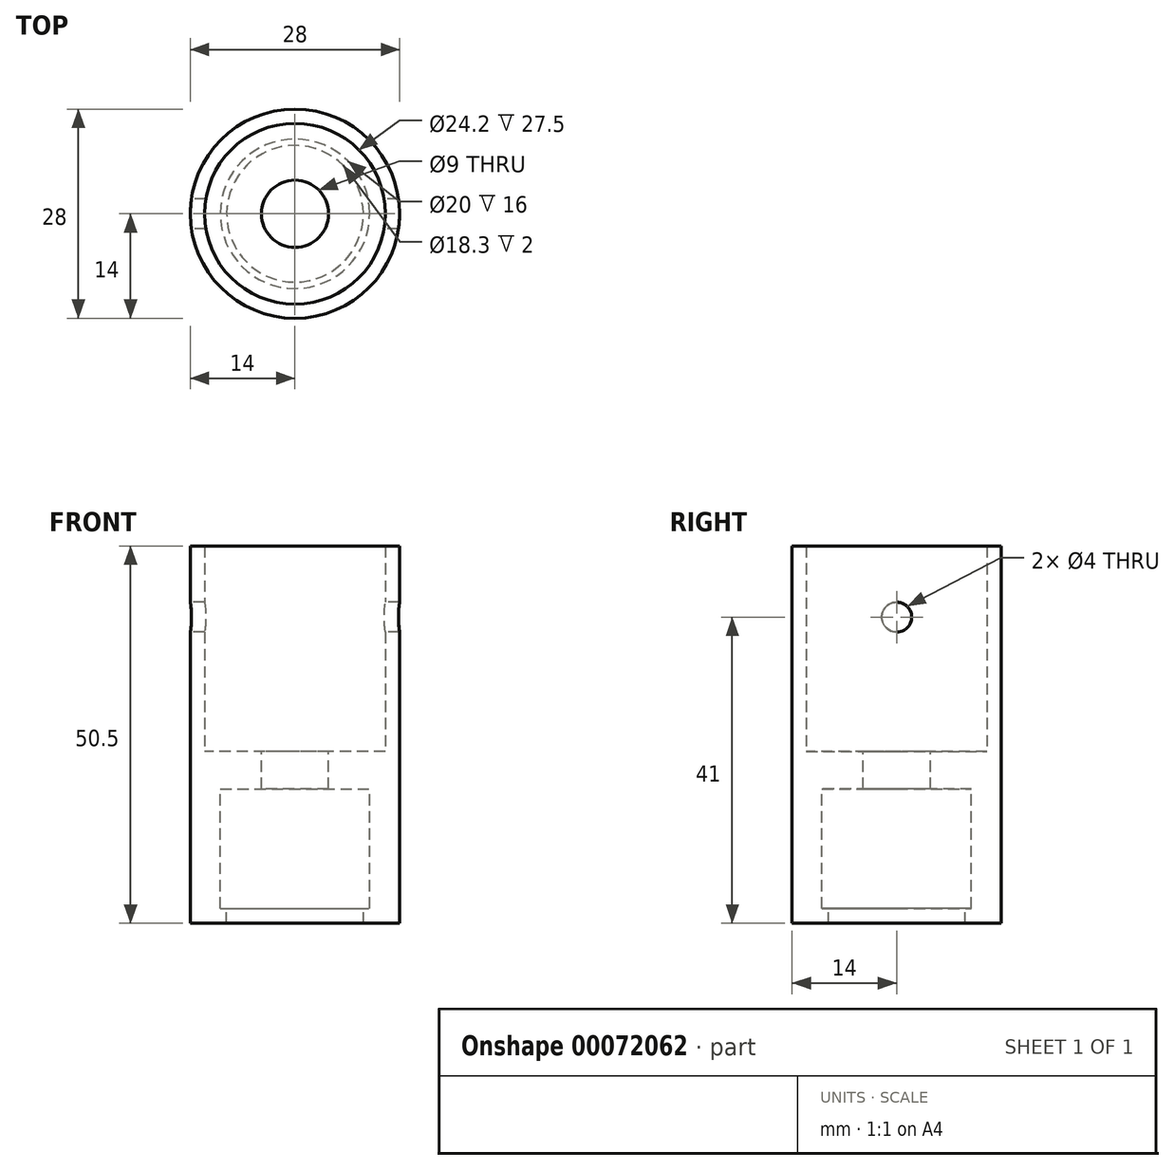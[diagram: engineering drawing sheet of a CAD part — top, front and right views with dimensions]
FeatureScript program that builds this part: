
annotation { "Feature Type Name" : "Feature", "Feature Type Description" : "" }
export const myFeature = defineFeature(function(context is Context, id is Id, definition is map)
    precondition{}
    {
        {
            var Q0;
            Q0=qCreatedBy(makeId("Top.planeOp"),FACE);
            var sketch = newSketch(context, id + "F0", { "sketchPlane" : qUnion([Q0])});
            skCircle(sketch, "E0", {"center": v(0, 0) * mm, "radius": 12.1 * mm});
            skCircle(sketch, "E1", {"center": v(0, 0) * mm, "radius": 14 * mm});
            skSolve(sketch);
        }
        {
            var Q0;
            Q0=qSketchRegion(id+"F0",true);
            extrude(context, id + "F1", {"entities" : qUnion([Q0]), "depth" : 27.5 * mm});
        }
        {
            var Q0;
            Q0=qCreatedBy(makeId("Top.planeOp"),FACE);
            var sketch = newSketch(context, id + "F2", { "sketchPlane" : qUnion([Q0])});
            skCircle(sketch, "E2", {"center": v(0, 0) * mm, "radius": 4.5 * mm});
            skCircle(sketch, "E3.0", {"center": v(0, 0) * mm, "radius": 14 * mm});
            skSolve(sketch);
        }
        {
            var Q0;
            Q0=qSketchRegion(id+"F2",true);
            extrude(context, id + "F3", {"entities" : qUnion([Q0]), "operationType" : NewBodyOperationType.ADD, "oppositeDirection" : true, "depth" : 5 * mm});
        }
        {
            var Q0;
            Q0=makeQuery(id+"F3.opExtrude","CAP_FACE",FACE,{"disambiguationData":[OSD([sQuery(id+"F2.wireOp",EDGE,"E2"),sQuery(id+"F2.wireOp",EDGE,"E3.0")])],"isStart":false});
            var sketch = newSketch(context, id + "F4", { "sketchPlane" : qUnion([Q0])});
            skCircle(sketch, "E4", {"center": v(0, 0) * mm, "radius": 10 * mm});
            skSolve(sketch);
        }
        {
            var Q0;
            Q0=makeQuery(id+"F4.imprint","IMPRINT",FACE,{"disambiguationData":[TD([[makeQuery(id+"F4.imprint","IMPRINT",EDGE,{"derivedFrom":sQuery(id+"F4.wireOp",EDGE,"E4")}),-1.0]])]});
            extrude(context, id + "F5", {"entities" : qUnion([Q0]), "operationType" : NewBodyOperationType.ADD, "depth" : 16 * mm});
        }
        {
            var Q0;
            Q0=makeQuery(id+"F5.opExtrude","CAP_FACE",FACE,{"disambiguationData":[OSD([sQuery(id+"F2.wireOp",EDGE,"E3.0"),sQuery(id+"F4.wireOp",EDGE,"E4")])],"isStart":false});
            var sketch = newSketch(context, id + "F6", { "sketchPlane" : qUnion([Q0])});
            skCircle(sketch, "E5", {"center": v(0, 0) * mm, "radius": 9.15 * mm});
            skCircle(sketch, "E6.0", {"center": v(0, 0) * mm, "radius": 14 * mm});
            skSolve(sketch);
        }
        {
            var Q0;
            Q0=qSketchRegion(id+"F6",true);
            extrude(context, id + "F7", {"entities" : qUnion([Q0]), "operationType" : NewBodyOperationType.ADD, "depth" : 2 * mm});
        }
        {
            var Q0;
            Q0=qCreatedBy(makeId("Right.planeOp"),FACE);
            var sketch = newSketch(context, id + "F8", { "sketchPlane" : qUnion([Q0])});
            skLineSegment(sketch, "E7.0", {"start": v(-14, 27.5) * mm, "end": v(14, 27.5) * mm});
            skCircle(sketch, "E8", {"center": v(0, 18) * mm, "radius": 2 * mm});
            skSolve(sketch);
        }
        {
            var Q0;
            Q0=qSketchRegion(id+"F8",true);
            extrude(context, id + "F9", {"entities" : qUnion([Q0]), "operationType" : NewBodyOperationType.REMOVE, "endBound" : BoundingType.SYMMETRIC, "depth" : 40 * mm});
        }
    });
